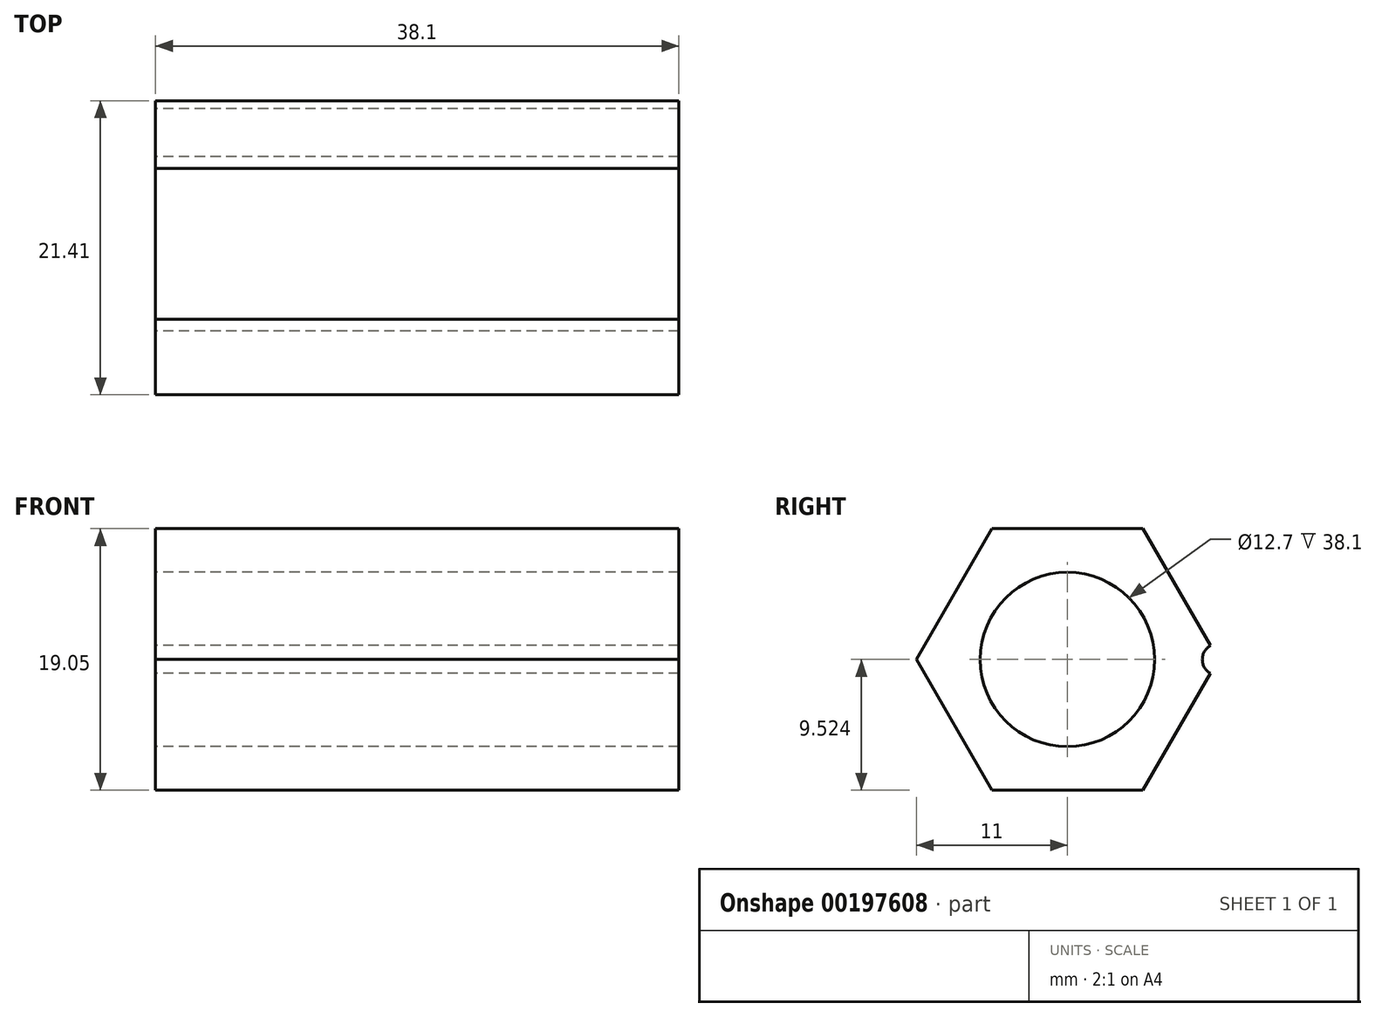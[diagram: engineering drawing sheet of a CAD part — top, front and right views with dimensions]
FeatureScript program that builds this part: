
annotation { "Feature Type Name" : "Feature", "Feature Type Description" : "" }
export const myFeature = defineFeature(function(context is Context, id is Id, definition is map)
    precondition{}
    {
        {
            var Q0;
            Q0=qCreatedBy(makeId("Right.planeOp"),FACE);
            var sketch = newSketch(context, id + "F0", { "sketchPlane" : qUnion([Q0])});
            skCircle(sketch, "E0.cCircle", {"center": v(0, 13.41) * mm, "radius": 9.53 * mm, "construction": true});
            skLineSegment(sketch, "E0.0", {"start": v(5.5, 3.89) * mm, "end": v(-5.5, 3.89) * mm});
            skLineSegment(sketch, "E0.1", {"start": v(-5.5, 3.89) * mm, "end": v(-11, 13.41) * mm});
            skLineSegment(sketch, "E0.2", {"start": v(-11, 13.41) * mm, "end": v(-5.5, 22.94) * mm});
            skLineSegment(sketch, "E0.3", {"start": v(-5.5, 22.94) * mm, "end": v(5.5, 22.94) * mm});
            skLineSegment(sketch, "E0.4", {"start": v(5.5, 22.94) * mm, "end": v(11, 13.41) * mm});
            skLineSegment(sketch, "E0.5", {"start": v(11, 13.41) * mm, "end": v(5.5, 3.89) * mm});
            skPoint(sketch, "E0.0.midPoint", {"position": v(0, 3.89) * mm});
            skCircle(sketch, "E1", {"center": v(0, 13.41) * mm, "radius": 6.35 * mm});
            skCircle(sketch, "E2", {"center": v(11, 13.41) * mm, "radius": 1.17 * mm});
            skSolve(sketch);
        }
        {
            var Q0;
            {var subQ6=sQuery(id+"F0.wireOp",EDGE,"E0.0");Q0=makeQuery(id+"F0.imprint","IMPRINT",FACE,{"disambiguationData":[TD([[makeQuery(id+"F0.imprint","IMPRINT",EDGE,{"derivedFrom":subQ6}),-1.0]])]});}
            extrude(context, id + "F1", {"entities" : qUnion([Q0]), "depth" : 38.1 * mm});
        }
    });
